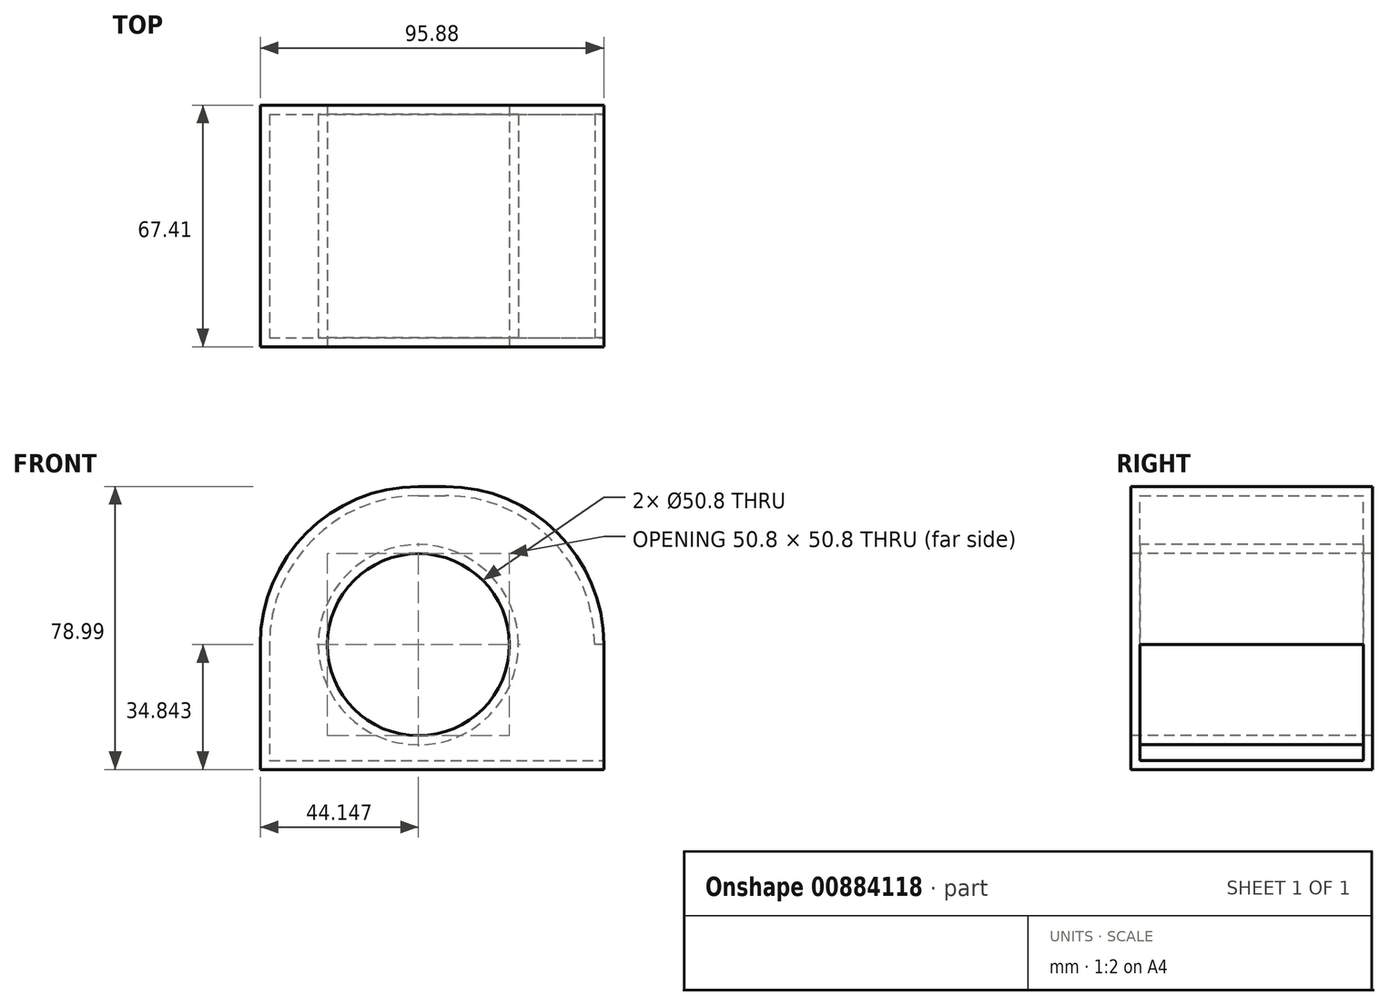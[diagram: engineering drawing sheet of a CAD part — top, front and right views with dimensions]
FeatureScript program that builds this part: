
annotation { "Feature Type Name" : "Feature", "Feature Type Description" : "" }
export const myFeature = defineFeature(function(context is Context, id is Id, definition is map)
    precondition{}
    {
        {
            var Q0;
            Q0=qCreatedBy(makeId("Top.planeOp"),FACE);
            var sketch = newSketch(context, id + "F0", { "sketchPlane" : qUnion([Q0])});
            skLineSegment(sketch, "E0.bottom", {"start": v(-88.07, -14.56) * mm, "end": v(7.81, -14.56) * mm});
            skLineSegment(sketch, "E0.top", {"start": v(-88.07, -81.97) * mm, "end": v(7.81, -81.97) * mm});
            skLineSegment(sketch, "E0.left", {"start": v(-88.07, -14.56) * mm, "end": v(-88.07, -81.97) * mm});
            skLineSegment(sketch, "E0.right", {"start": v(7.81, -14.56) * mm, "end": v(7.81, -81.97) * mm});
            skSolve(sketch);
        }
        {
            var Q0;
            Q0 = qSketchRegion(id + "F0", true);
            extrude(context, id + "F1", {"entities" : qUnion([Q0]), "depth" : 79 * mm, "offsetDistance" : 25.4 * mm});
        }
        {
            var Q0;
            Q0=makeQuery(id+"F1.opExtrude","CAP_EDGE",EDGE,{"disambiguationData":[OSD([sQuery(id+"F0.wireOp",EDGE,"E0.left")])],"isStart":false});
            var Q1;
            Q1=makeQuery(id+"F1.opExtrude","CAP_EDGE",EDGE,{"disambiguationData":[OSD([sQuery(id+"F0.wireOp",EDGE,"E0.right")])],"isStart":false});
            fillet(context, id + "F2", {"entities" : qUnion([Q0, Q1]), "radius" : 44.15 * mm, "tangentPropagation" : true, "allowEdgeOverflow" : false});
        }
        {
            var Q0;
            Q0=makeQuery(id+"F1.opExtrude","SWEPT_FACE",FACE,{"disambiguationData":[OSD([sQuery(id+"F0.wireOp",EDGE,"E0.top")])]});
            var sketch = newSketch(context, id + "F3", { "sketchPlane" : qUnion([Q0])});
            skCircle(sketch, "E1", {"center": v(-43.92, 34.84) * mm, "radius": 18.23 * mm});
            skSolve(sketch);
        }
        {
            var Q0;
            Q0=sQuery(id+"F3.wireOp",VERTEX,"E1.center");
            var Q1;
            Q1=makeQuery(id+"F1.opExtrude","SWEPT_BODY",BODY,{"disambiguationData":[OSD([sQuery(id+"F0.wireOp",EDGE,"E0.bottom"),sQuery(id+"F0.wireOp",EDGE,"E0.top"),sQuery(id+"F0.wireOp",EDGE,"E0.left"),sQuery(id+"F0.wireOp",EDGE,"E0.right")])]});
            hole(context, id + "F4", {"style" : HoleStyle.SIMPLE, "endStyle" : HoleEndStyle.THROUGH, "holeDiameter" : 50.8 * mm, "majorDiameter" : 6.35 * mm, "isTappedThrough" : true, "tappedDepth" : 12.7 * mm, "tapClearance" : 3, "locations" : qUnion([Q0]), "scope" : qUnion([Q1])});
        }
        {
            var Q0;
            Q0=makeQuery(id+"F1.opExtrude","SWEPT_FACE",FACE,{"disambiguationData":[OSD([sQuery(id+"F0.wireOp",EDGE,"E0.right")])]});
            shell(context, id + "F5", {"entities" : qUnion([Q0]), "thickness" : 2.54 * mm});
        }
    });
